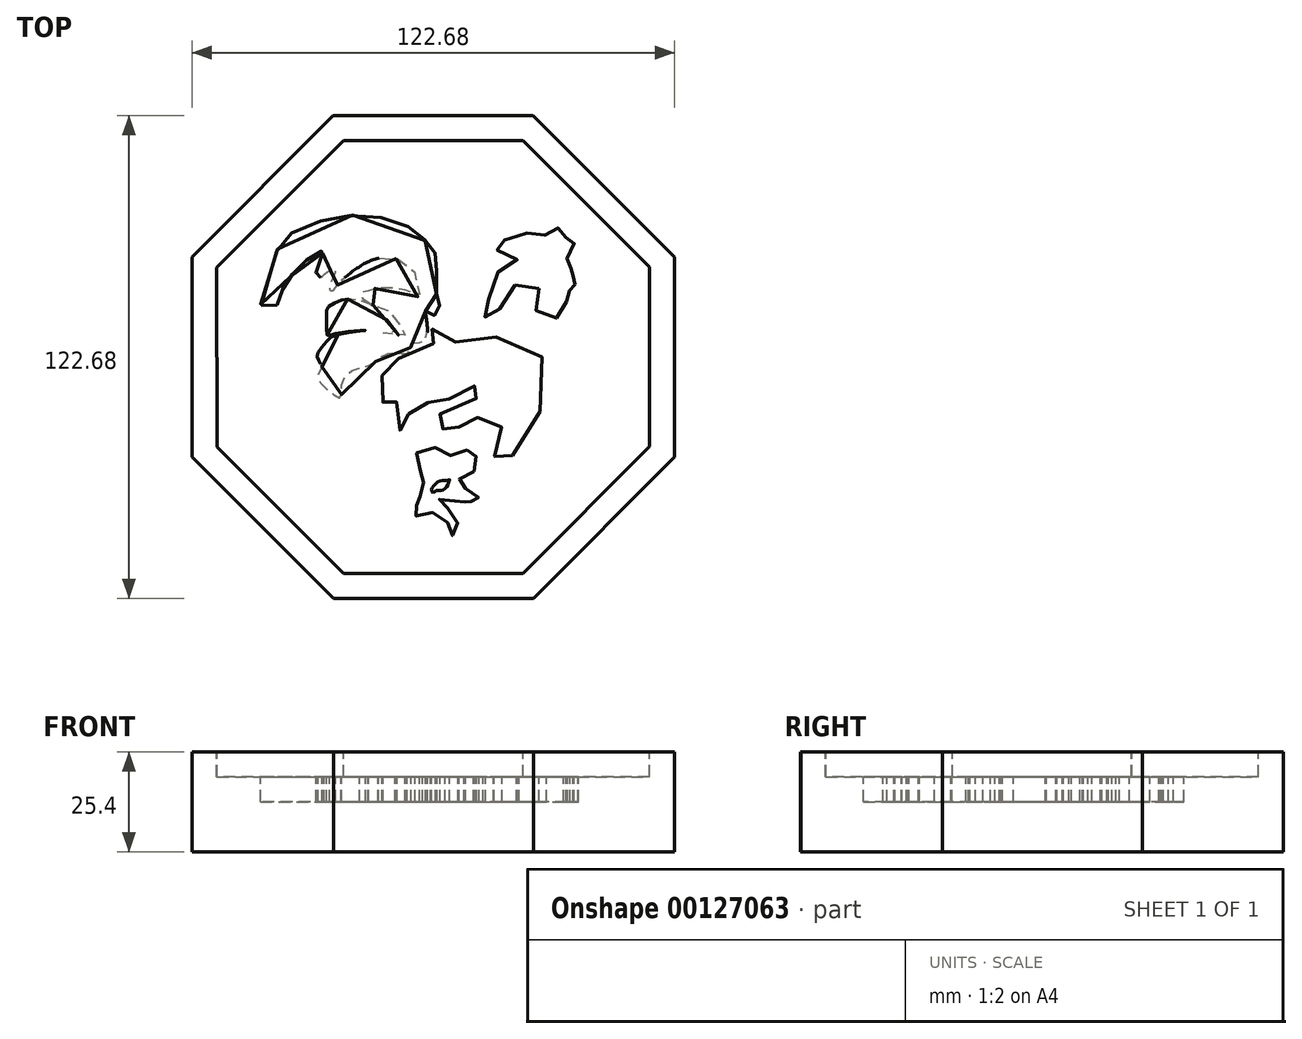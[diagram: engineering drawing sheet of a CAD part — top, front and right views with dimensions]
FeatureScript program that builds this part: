
annotation { "Feature Type Name" : "Feature", "Feature Type Description" : "" }
export const myFeature = defineFeature(function(context is Context, id is Id, definition is map)
    precondition{}
    {
        {
            var Q0;
            Q0=qCreatedBy(makeId("Top.planeOp"),FACE);
            var sketch = newSketch(context, id + "F0", { "sketchPlane" : qUnion([Q0])});
            skCircle(sketch, "E0.cCircle", {"center": v(0, 0) * mm, "radius": 61.32 * mm, "construction": true});
            skLineSegment(sketch, "E0.0", {"start": v(-61.3, -25.44) * mm, "end": v(-61.34, 25.36) * mm});
            skLineSegment(sketch, "E0.1", {"start": v(-61.34, 25.36) * mm, "end": v(-25.44, 61.3) * mm});
            skLineSegment(sketch, "E0.2", {"start": v(-25.44, 61.3) * mm, "end": v(25.36, 61.34) * mm});
            skLineSegment(sketch, "E0.3", {"start": v(25.36, 61.34) * mm, "end": v(61.3, 25.44) * mm});
            skLineSegment(sketch, "E0.4", {"start": v(61.3, 25.44) * mm, "end": v(61.34, -25.36) * mm});
            skLineSegment(sketch, "E0.5", {"start": v(61.34, -25.36) * mm, "end": v(25.44, -61.3) * mm});
            skLineSegment(sketch, "E0.6", {"start": v(25.44, -61.3) * mm, "end": v(-25.36, -61.34) * mm});
            skLineSegment(sketch, "E0.7", {"start": v(-25.36, -61.34) * mm, "end": v(-61.3, -25.44) * mm});
            skPoint(sketch, "E0.0.midPoint", {"position": v(-61.32, -0.04) * mm});
            skSolve(sketch);
        }
        {
            var Q0;
            Q0=qSketchRegion(id+"F0",true);
            extrude(context, id + "F1", {"entities" : qUnion([Q0]), "depth" : 25.4 * mm});
        }
        {
            var Q0;
            Q0=makeQuery(id+"F1.opExtrude","CAP_FACE",FACE,{"disambiguationData":[OSD([sQuery(id+"F0.wireOp",EDGE,"E0.0"),sQuery(id+"F0.wireOp",EDGE,"E0.1"),sQuery(id+"F0.wireOp",EDGE,"E0.2"),sQuery(id+"F0.wireOp",EDGE,"E0.3"),sQuery(id+"F0.wireOp",EDGE,"E0.4"),sQuery(id+"F0.wireOp",EDGE,"E0.5"),sQuery(id+"F0.wireOp",EDGE,"E0.6"),sQuery(id+"F0.wireOp",EDGE,"E0.7")])],"isStart":false});
            var sketch = newSketch(context, id + "F2", { "sketchPlane" : qUnion([Q0])});
            skLineSegment(sketch, "E1.0", {"start": v(-54.96, -22.8) * mm, "end": v(-54.99, 22.73) * mm});
            skLineSegment(sketch, "E1.1", {"start": v(-22.73, -54.99) * mm, "end": v(-54.96, -22.8) * mm});
            skLineSegment(sketch, "E1.2", {"start": v(-54.99, 22.73) * mm, "end": v(-22.8, 54.96) * mm});
            skLineSegment(sketch, "E1.3", {"start": v(22.8, -54.96) * mm, "end": v(-22.73, -54.99) * mm});
            skLineSegment(sketch, "E1.4", {"start": v(-22.8, 54.96) * mm, "end": v(22.73, 54.99) * mm});
            skLineSegment(sketch, "E1.5", {"start": v(22.73, 54.99) * mm, "end": v(54.96, 22.8) * mm});
            skLineSegment(sketch, "E1.6", {"start": v(54.96, 22.8) * mm, "end": v(54.99, -22.73) * mm});
            skLineSegment(sketch, "E1.7", {"start": v(54.99, -22.73) * mm, "end": v(22.8, -54.96) * mm});
            skSolve(sketch);
        }
        {
            var Q0;
            Q0=qSketchRegion(id+"F2",true);
            extrude(context, id + "F3", {"entities" : qUnion([Q0]), "operationType" : NewBodyOperationType.REMOVE, "oppositeDirection" : true, "depth" : 6.35 * mm});
        }
        {
            var Q0;
            Q0=makeQuery(id+"F3.boolean.opBoolean","COPY",FACE,{"derivedFrom":makeQuery(id+"F3.opExtrude","CAP_FACE",FACE,{"disambiguationData":[OSD([sQuery(id+"F2.wireOp",EDGE,"E1.0"),sQuery(id+"F2.wireOp",EDGE,"E1.1"),sQuery(id+"F2.wireOp",EDGE,"E1.2"),sQuery(id+"F2.wireOp",EDGE,"E1.3"),sQuery(id+"F2.wireOp",EDGE,"E1.4"),sQuery(id+"F2.wireOp",EDGE,"E1.5"),sQuery(id+"F2.wireOp",EDGE,"E1.6"),sQuery(id+"F2.wireOp",EDGE,"E1.7")])],"isStart":false})});
            var sketch = newSketch(context, id + "F4", { "sketchPlane" : qUnion([Q0])});
            skFitSpline(sketch, "E2", {"points": [v(-1.97, 11.62) * mm, v(-1.17, 10.83) * mm, v(0, 10.51) * mm, v(1.04, 11.07) * mm, v(1.6, 12.81) * mm, v(1.52, 14.95) * mm, v(0.8, 16.22) * mm, v(0.89, 22.17) * mm, v(0.73, 25.9) * mm, v(-0.94, 28.27) * mm, v(-3.4, 31.04) * mm, v(-8.78, 34.13) * mm, v(-19.17, 36.04) * mm, v(-29, 34.37) * mm, v(-37.95, 29.93) * mm, v(-40.41, 24.78) * mm, v(-42, 18.92) * mm, v(-43.18, 15.27) * mm, v(-43.9, 13.53) * mm, v(-42.79, 12.81) * mm, v(-39.78, 13.2) * mm, v(-38.83, 15.74) * mm, v(-37.24, 19.07) * mm, v(-34.78, 22.17) * mm, v(-31.45, 25.18) * mm, v(-28.6, 26.76) * mm, v(-27.73, 27.32) * mm, v(-27.97, 26.76) * mm, v(-29, 24.15) * mm, v(-29.79, 20.9) * mm, v(-29.16, 19.63) * mm, v(-28.68, 20.03) * mm, v(-26.78, 21.69) * mm, v(-24.95, 22.09) * mm, v(-25.11, 21.13) * mm, v(-26.14, 18.6) * mm, v(-26.3, 17.1) * mm, v(-25.5, 16.85) * mm, v(-24.4, 18.28) * mm, v(-20.91, 21.45) * mm, v(-16, 24.46) * mm, v(-9.81, 25.1) * mm, v(-4.5, 21.13) * mm, v(-4.19, 18.68) * mm, v(-3.63, 17.4) * mm, v(-3.71, 15.19) * mm, v(-4.27, 15.74) * mm, v(-5.84, 16.89) * mm, v(-7.9, 17.04) * mm, v(-11.16, 17.65) * mm, v(-14.05, 17.48) * mm, v(-16.63, 16.93) * mm, v(-16.4, 16.46) * mm, v(-18.14, 16.38) * mm, v(-18.77, 15.59) * mm, v(-17.74, 14.64) * mm, v(-15.2, 13.13) * mm, v(-11.08, 11.54) * mm, v(-8, 7.34) * mm, v(-7.2, 5.6) * mm, v(-8.78, 5.52) * mm, v(-11.16, 6) * mm, v(-12.75, 6.15) * mm, v(-10.05, 6.55) * mm, v(-9.74, 7.18) * mm, v(-11.32, 8.93) * mm, v(-14.02, 11.62) * mm, v(-16.31, 13.53) * mm, v(-17.9, 14.16) * mm, v(-20.36, 14.71) * mm, v(-23.05, 14.48) * mm, v(-26.7, 12.73) * mm, v(-27.17, 10.99) * mm, v(-27.17, 7.65) * mm, v(-26.93, 5.43) * mm, v(-25.54, 5.83) * mm, v(-17.26, 6.74) * mm, v(-23.6, 5.87) * mm, v(-27.1, 4.01) * mm, v(-29.3, 0.95) * mm, v(-29.47, 0) * mm, v(-28.84, -1.46) * mm, v(-28.28, -2.4) * mm, v(-29.31, -4.86) * mm, v(-27.96, -7.37) * mm, v(-25.26, -9.59) * mm, v(-23.53, -10.33) * mm, v(-23.37, -8.27) * mm, v(-22.1, -4.47) * mm, v(-18.73, -2.73) * mm, v(-15.68, -1.85) * mm, v(-13.22, 0) * mm, v(-11.16, 0.92) * mm, v(-9.1, 1) * mm, v(-6.8, 0.84) * mm, v(-6.17, 1.4) * mm, v(-5.14, 3.46) * mm, v(-3.7, 3.69) * mm, v(-2.2, 4.08) * mm, v(-1.57, 8.3) * mm, v(-1.97, 11.62) * mm]});
            skFitSpline(sketch, "E3", {"points": [v(0, -34.53) * mm, v(0.6, -34.03) * mm, v(1.94, -33.93) * mm, v(2.8, -33.63) * mm, v(3.82, -32.23) * mm, v(3.94, -31.48) * mm, v(4.14, -31.18) * mm, v(3.54, -31.38) * mm, v(2.7, -31.33) * mm, v(1.24, -31.63) * mm, v(0, -32.93) * mm, v(-0.5, -33.73) * mm, v(0, -34.53) * mm]});
            skFitSpline(sketch, "E4", {"points": [v(10.4, -29.15) * mm, v(10.27, -27.35) * mm, v(10.33, -26) * mm, v(10.98, -24.9) * mm, v(10.69, -23.37) * mm, v(9.31, -23.37) * mm, v(7.38, -24.27) * mm, v(6.29, -24.9) * mm, v(4.07, -25) * mm, v(2.34, -24.33) * mm, v(0.8, -23.15) * mm, v(-0.95, -22.95) * mm, v(-3.6, -23.6) * mm, v(-4.65, -25.8) * mm, v(-4.25, -27.84) * mm, v(-2.55, -29.79) * mm, v(-2.04, -30.55) * mm, v(-2.06, -31.25) * mm, v(-2.55, -32.08) * mm, v(-3.4, -33.33) * mm, v(-3.46, -34.52) * mm, v(-3.3, -35.88) * mm, v(-2.7, -36.63) * mm, v(-3, -37.13) * mm, v(-4.3, -37.73) * mm, v(-5.35, -38.82) * mm, v(-5.45, -40.17) * mm, v(-3.85, -40.32) * mm, v(-2.75, -39.72) * mm, v(-0.7, -39.47) * mm, v(1.1, -39.82) * mm, v(3, -41.07) * mm, v(3.79, -42.72) * mm, v(3.89, -44.47) * mm, v(4.24, -45.02) * mm, v(5.29, -45.42) * mm, v(5.69, -44.47) * mm, v(6.04, -43.12) * mm, v(6.09, -40.72) * mm, v(4.64, -39.12) * mm, v(3, -38.03) * mm, v(1.2, -36.88) * mm, v(0.94, -36.58) * mm, v(2.04, -35.98) * mm, v(3.89, -35.73) * mm, v(5.07, -36.21) * mm, v(5.99, -37.03) * mm, v(6.79, -37.58) * mm, v(7.66, -37.37) * mm, v(8.13, -36.48) * mm, v(7.78, -35.58) * mm, v(8.63, -36.07) * mm, v(9.64, -36.69) * mm, v(10.08, -37.13) * mm, v(11.13, -37.23) * mm, v(11.57, -35.96) * mm, v(10.91, -35.08) * mm, v(9.73, -34.23) * mm, v(8.18, -33.43) * mm, v(7.58, -33.03) * mm, v(6.79, -32.28) * mm, v(6.59, -31.38) * mm, v(6.94, -30.49) * mm, v(8.43, -30.14) * mm, v(10.4, -29.15) * mm]});
            skFitSpline(sketch, "E5", {"points": [v(26.85, 17.34) * mm, v(24.69, 18.6) * mm, v(20.59, 18.09) * mm, v(17.8, 13.99) * mm, v(16.44, 11.54) * mm, v(15.3, 10.36) * mm, v(13.47, 10.22) * mm, v(12.67, 10.31) * mm, v(13.28, 11.82) * mm, v(14.13, 15.12) * mm, v(15.26, 19.7) * mm, v(18.14, 22.85) * mm, v(21.53, 24.22) * mm, v(20.4, 25.4) * mm, v(18.09, 26.48) * mm, v(15.78, 27.52) * mm, v(15.4, 28.55) * mm, v(16.25, 29.21) * mm, v(20.2, 29.82) * mm, v(21.76, 29.64) * mm, v(21.58, 30.06) * mm, v(21.3, 31.66) * mm, v(21.1, 32.04) * mm, v(21.81, 31.76) * mm, v(24.64, 31.29) * mm, v(27.6, 30.3) * mm, v(27.99, 30.34) * mm, v(28.98, 32) * mm, v(30.34, 33.22) * mm, v(31.33, 33.12) * mm, v(32.23, 31.33) * mm, v(32.51, 29.73) * mm, v(33.6, 30.34) * mm, v(36.75, 30.67) * mm, v(36.61, 30.1) * mm, v(35.34, 28.32) * mm, v(34.35, 27.1) * mm, v(33.74, 25.4) * mm, v(34.63, 24.55) * mm, v(35.67, 23.65) * mm, v(35.57, 23.13) * mm, v(34.87, 22.47) * mm, v(34.3, 22.14) * mm, v(34.11, 21.48) * mm, v(34.68, 21.2) * mm, v(35.48, 20.73) * mm, v(35.39, 20.16) * mm, v(35.06, 19.7) * mm, v(34.68, 19.46) * mm, v(35.95, 18.42) * mm, v(36.52, 17.67) * mm, v(36.85, 17.29) * mm, v(35.86, 17) * mm, v(33.78, 16.82) * mm, v(33.12, 16.72) * mm, v(33.36, 15.45) * mm, v(33.97, 12.9) * mm, v(32.98, 10.93) * mm, v(30.77, 9.75) * mm, v(28.03, 9.8) * mm, v(25.91, 12.3) * mm, v(26.1, 15.45) * mm, v(26.85, 17.34) * mm]});
            skFitSpline(sketch, "E6", {"points": [v(5.66, 3.83) * mm, v(10.82, 4.08) * mm, v(15.22, 4.96) * mm, v(23.65, 4.14) * mm, v(28.37, -2.02) * mm, v(28, -11.65) * mm, v(24.97, -17.56) * mm, v(20.13, -24.98) * mm, v(18.27, -27.12) * mm, v(16.9, -27.22) * mm, v(15.96, -26.13) * mm, v(15.34, -24.2) * mm, v(16.05, -21.33) * mm, v(17.18, -18.17) * mm, v(17.46, -17.42) * mm, v(16.15, -16) * mm, v(12.9, -15.01) * mm, v(9.74, -16.24) * mm, v(8.04, -17.98) * mm, v(7.61, -18.69) * mm, v(6.86, -18.08) * mm, v(5.45, -17.18) * mm, v(3.7, -16.94) * mm, v(3, -17.42) * mm, v(2.95, -18.26) * mm, v(1.58, -17.75) * mm, v(0, -16.2) * mm, v(-0.54, -15.53) * mm, v(1.1, -14.68) * mm, v(5.73, -12.99) * mm, v(9.74, -11.1) * mm, v(12.61, -9.6) * mm, v(13.32, -8.55) * mm, v(12.61, -7.75) * mm, v(10.11, -7.37) * mm, v(8.37, -8.32) * mm, v(7.76, -8.7) * mm, v(4.5, -10.3) * mm, v(2.15, -11.9) * mm, v(0, -13.08) * mm, v(-0.59, -12.42) * mm, v(-1.81, -11.1) * mm, v(-2.57, -10.91) * mm, v(-4.03, -11.71) * mm, v(-6.05, -13.98) * mm, v(-6.8, -17.37) * mm, v(-6.76, -19.3) * mm, v(-7.7, -19.2) * mm, v(-8.83, -18.12) * mm, v(-9.35, -16.14) * mm, v(-9.54, -12.75) * mm, v(-9.26, -10.77) * mm, v(-9.26, -10.11) * mm, v(-9.68, -10.82) * mm, v(-11.29, -11.95) * mm, v(-13.31, -11) * mm, v(-14.07, -9.07) * mm, v(-13.4, -6.48) * mm, v(-13.08, -4.4) * mm, v(-13.88, -3.04) * mm, v(-12, -1.3) * mm, v(-7.9, 0) * mm, v(-4.03, 2) * mm, v(0, 3.42) * mm, v(0.36, 4.08) * mm, v(0.5, 4.92) * mm, v(0, 5.58) * mm, v(-0.59, 6.06) * mm, v(-0.5, 6.95) * mm, v(2.34, 7.38) * mm, v(4.6, 6.24) * mm, v(5.66, 3.83) * mm]});
            skSolve(sketch);
        }
        {
            var Q0;
            Q0 = qSketchRegion(id + "F4", true);
            extrude(context, id + "F5", {"entities" : qUnion([Q0]), "operationType" : NewBodyOperationType.REMOVE, "oppositeDirection" : true, "depth" : 6.35 * mm});
        }
    });
